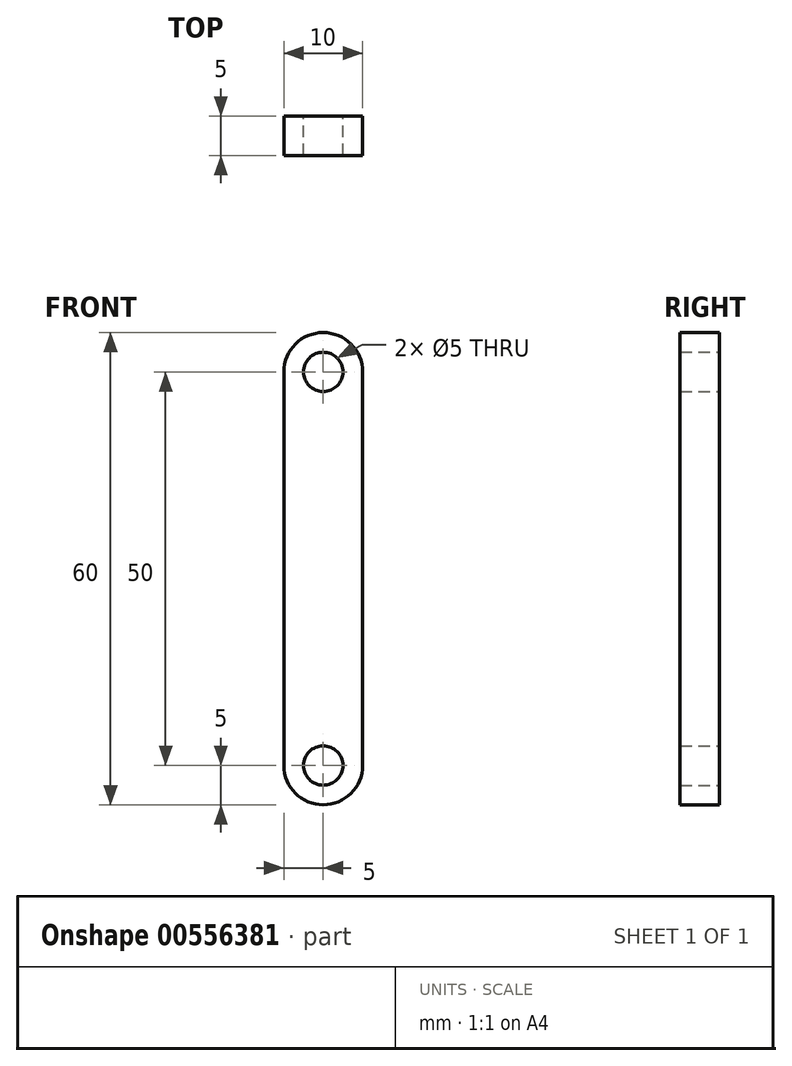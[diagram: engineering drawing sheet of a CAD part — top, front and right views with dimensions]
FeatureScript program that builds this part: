
annotation { "Feature Type Name" : "Feature", "Feature Type Description" : "" }
export const myFeature = defineFeature(function(context is Context, id is Id, definition is map)
    precondition{}
    {
        {
            var Q0;
            Q0=qCreatedBy(makeId("Front.planeOp"),FACE);
            var sketch = newSketch(context, id + "F0", { "sketchPlane" : qUnion([Q0])});
            skArc(sketch, "E0", {"start": v(-5, 0) * mm, "mid": v(0, -5) * mm, "end": v(5, 0) * mm});
            skArc(sketch, "E1", {"start": v(5, 50) * mm, "mid": v(0, 55) * mm, "end": v(-5, 50) * mm});
            skCircle(sketch, "E2", {"center": v(0, 50) * mm, "radius": 2.5 * mm});
            skCircle(sketch, "E3", {"center": v(0, 0) * mm, "radius": 2.5 * mm});
            skLineSegment(sketch, "E4", {"start": v(5, 50) * mm, "end": v(5, 0) * mm});
            skLineSegment(sketch, "E5", {"start": v(-5, 50) * mm, "end": v(-5, 0) * mm});
            skSolve(sketch);
        }
        {
            var Q0;
            Q0=makeQuery(id+"F0.imprint","IMPRINT",FACE,{"disambiguationData":[TD([[makeQuery(id+"F0.imprint","IMPRINT",EDGE,{"derivedFrom":sQuery(id+"F0.wireOp",EDGE,"E0")}),1.0]])]});
            extrude(context, id + "F1", {"entities" : qUnion([Q0]), "depth" : 5 * mm, "offsetDistance" : 25 * mm});
        }
    });
